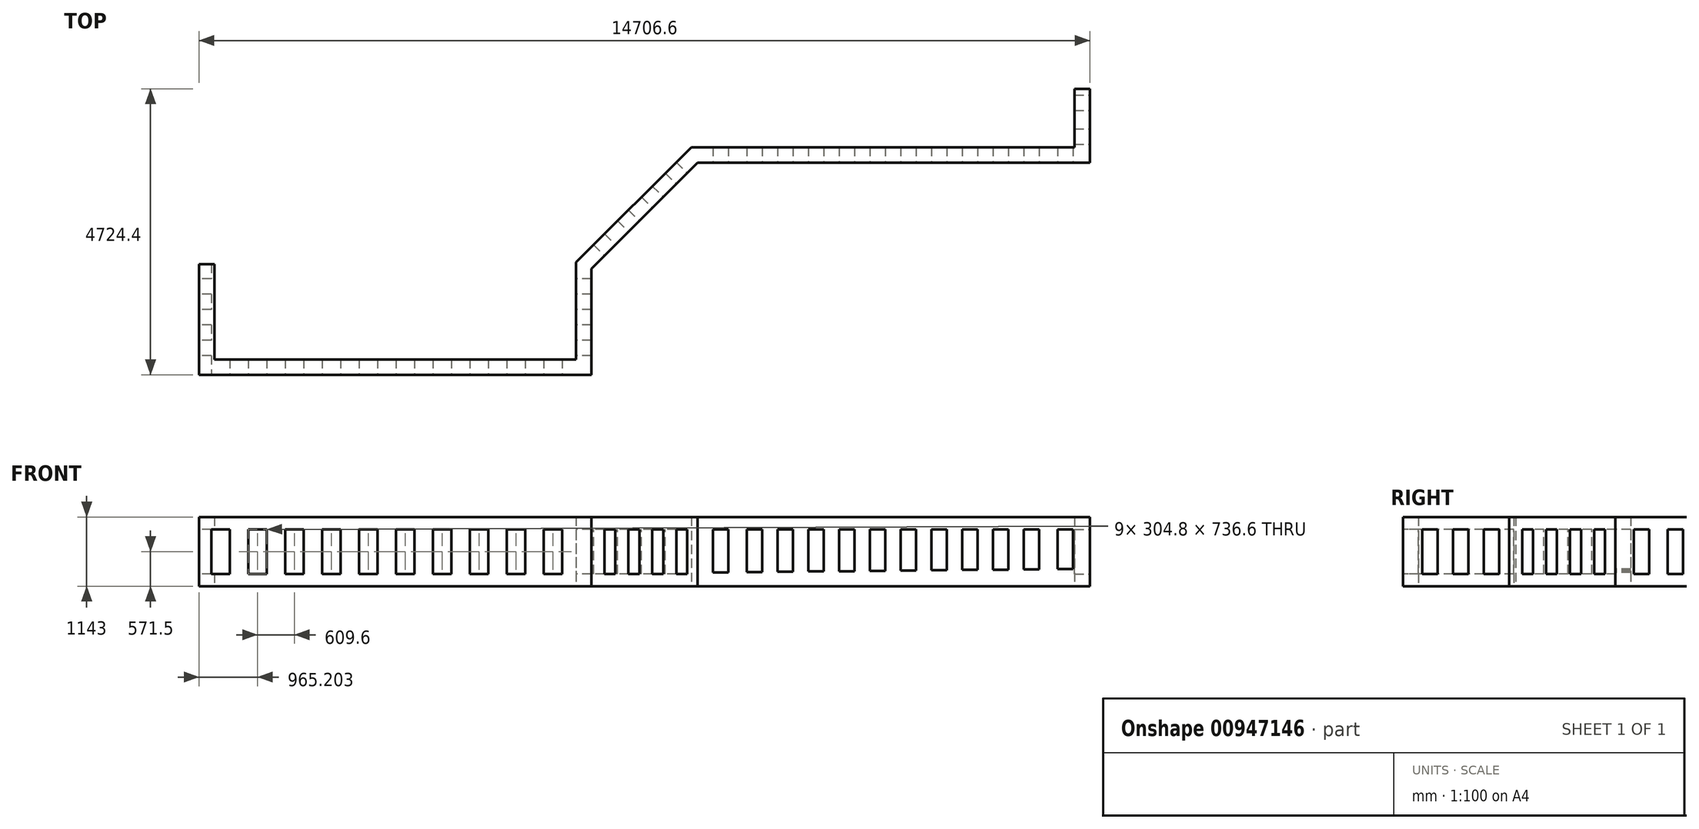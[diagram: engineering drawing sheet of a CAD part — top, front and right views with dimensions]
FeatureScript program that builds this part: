
annotation { "Feature Type Name" : "Feature", "Feature Type Description" : "" }
export const myFeature = defineFeature(function(context is Context, id is Id, definition is map)
    precondition{}
    {
        {
            var Q0;
            Q0=qCreatedBy(makeId("Top.planeOp"),FACE);
            var sketch = newSketch(context, id + "F0", { "sketchPlane" : qUnion([Q0])});
            skLineSegment(sketch, "E0.bottom", {"start": v(-9577.35, -1588.74) * mm, "end": v(-3100.35, -1588.74) * mm});
            skLineSegment(sketch, "E0.top", {"start": v(-9323.35, -1334.74) * mm, "end": v(-3354.35, -1334.74) * mm});
            skLineSegment(sketch, "E0.left", {"start": v(-9577.35, -1588.74) * mm, "end": v(-9577.35, -1334.74) * mm});
            skLineSegment(sketch, "E1.left", {"start": v(-3100.35, -1588.74) * mm, "end": v(-3100.35, 163.86) * mm});
            skLineSegment(sketch, "E2.top", {"start": v(-1347.75, 1916.46) * mm, "end": v(5129.25, 1916.46) * mm});
            skLineSegment(sketch, "E3", {"start": v(-3354.35, -1334.74) * mm, "end": v(-3354.35, 269.07) * mm});
            skLineSegment(sketch, "E4", {"start": v(-1347.75, 1916.46) * mm, "end": v(-3100.35, 163.86) * mm});
            skLineSegment(sketch, "E5", {"start": v(4875.25, 2170.46) * mm, "end": v(-1452.96, 2170.46) * mm});
            skLineSegment(sketch, "E6", {"start": v(-3354.35, 269.07) * mm, "end": v(-1452.96, 2170.46) * mm});
            skLineSegment(sketch, "E7.bottom", {"start": v(-9577.35, -1588.74) * mm, "end": v(-9323.35, -1588.74) * mm});
            skLineSegment(sketch, "E7.top", {"start": v(-9577.35, 240.06) * mm, "end": v(-9323.35, 240.06) * mm});
            skLineSegment(sketch, "E7.left", {"start": v(-9577.35, -1334.74) * mm, "end": v(-9577.35, 240.06) * mm});
            skLineSegment(sketch, "E7.right", {"start": v(-9323.35, -1334.74) * mm, "end": v(-9323.35, 240.06) * mm});
            skLineSegment(sketch, "E8.top", {"start": v(5129.25, 3135.66) * mm, "end": v(4875.25, 3135.66) * mm});
            skLineSegment(sketch, "E8.left", {"start": v(5129.25, 1916.46) * mm, "end": v(5129.25, 3135.66) * mm});
            skLineSegment(sketch, "E8.right", {"start": v(4875.25, 2170.46) * mm, "end": v(4875.25, 3135.66) * mm});
            skSolve(sketch);
        }
        {
            var Q0;
            Q0=makeQuery(id+"F0.imprint","IMPRINT",FACE,{"disambiguationData":[TD([[makeQuery(id+"F0.imprint","IMPRINT",EDGE,{"derivedFrom":sQuery(id+"F0.wireOp",EDGE,"E0.top")}),-1.0]])]});
            extrude(context, id + "F1", {"entities" : qUnion([Q0]), "depth" : 1143 * mm, "offsetDistance" : 25.4 * mm});
        }
        {
            var Q0;
            Q0=makeQuery(id+"F1.opExtrude","SWEPT_FACE",FACE,{"disambiguationData":[OSD([sQuery(id+"F0.wireOp",EDGE,"E0.bottom")])]});
            var sketch = newSketch(context, id + "F2", { "sketchPlane" : qUnion([Q0])});
            skLineSegment(sketch, "E9.bottom", {"start": v(-9374.15, 939.8) * mm, "end": v(-9069.35, 939.8) * mm});
            skLineSegment(sketch, "E9.top", {"start": v(-9374.15, 203.2) * mm, "end": v(-9069.35, 203.2) * mm});
            skLineSegment(sketch, "E9.left", {"start": v(-9374.15, 939.8) * mm, "end": v(-9374.15, 203.2) * mm});
            skLineSegment(sketch, "E9.right", {"start": v(-9069.35, 939.8) * mm, "end": v(-9069.35, 203.2) * mm});
            skLineSegment(sketch, "E10.1.0.0", {"start": v(-8459.75, 939.8) * mm, "end": v(-8459.75, 203.2) * mm});
            skLineSegment(sketch, "E10.1.0.1", {"start": v(-8764.55, 939.8) * mm, "end": v(-8764.55, 203.2) * mm});
            skLineSegment(sketch, "E10.2.0.0", {"start": v(-7850.15, 939.8) * mm, "end": v(-7850.15, 203.2) * mm});
            skLineSegment(sketch, "E10.2.0.1", {"start": v(-8154.95, 939.8) * mm, "end": v(-8154.95, 203.2) * mm});
            skLineSegment(sketch, "E10.3.0.0", {"start": v(-7240.55, 939.8) * mm, "end": v(-7240.55, 203.2) * mm});
            skLineSegment(sketch, "E10.3.0.1", {"start": v(-7545.35, 939.8) * mm, "end": v(-7545.35, 203.2) * mm});
            skLineSegment(sketch, "E10.4.0.0", {"start": v(-6630.95, 939.8) * mm, "end": v(-6630.95, 203.2) * mm});
            skLineSegment(sketch, "E10.4.0.1", {"start": v(-6935.75, 939.8) * mm, "end": v(-6935.75, 203.2) * mm});
            skLineSegment(sketch, "E10.5.0.0", {"start": v(-6021.35, 939.8) * mm, "end": v(-6021.35, 203.2) * mm});
            skLineSegment(sketch, "E10.5.0.1", {"start": v(-6326.15, 939.8) * mm, "end": v(-6326.15, 203.2) * mm});
            skLineSegment(sketch, "E10.6.0.0", {"start": v(-5411.75, 939.8) * mm, "end": v(-5411.75, 203.2) * mm});
            skLineSegment(sketch, "E10.6.0.1", {"start": v(-5716.55, 939.8) * mm, "end": v(-5716.55, 203.2) * mm});
            skLineSegment(sketch, "E10.7.0.0", {"start": v(-4802.15, 939.8) * mm, "end": v(-4802.15, 203.2) * mm});
            skLineSegment(sketch, "E10.7.0.1", {"start": v(-5106.95, 939.8) * mm, "end": v(-5106.95, 203.2) * mm});
            skLineSegment(sketch, "E10.8.0.0", {"start": v(-4192.55, 939.8) * mm, "end": v(-4192.55, 203.2) * mm});
            skLineSegment(sketch, "E10.8.0.1", {"start": v(-4497.35, 939.8) * mm, "end": v(-4497.35, 203.2) * mm});
            skLineSegment(sketch, "E10.9.0.0", {"start": v(-3582.95, 939.8) * mm, "end": v(-3582.95, 203.2) * mm});
            skLineSegment(sketch, "E10.9.0.1", {"start": v(-3887.75, 939.8) * mm, "end": v(-3887.75, 203.2) * mm});
            skLineSegment(sketch, "E11", {"start": v(-8764.55, 939.8) * mm, "end": v(-8459.75, 939.8) * mm});
            skLineSegment(sketch, "E12", {"start": v(-8764.55, 203.2) * mm, "end": v(-8459.75, 203.2) * mm});
            skPoint(sketch, "E13.orphan", {"position": v(-8991.86, 203.2) * mm});
            skLineSegment(sketch, "E14.trimOffspring", {"start": v(-8154.95, 203.2) * mm, "end": v(-7850.15, 203.2) * mm});
            skLineSegment(sketch, "E15.trimOffspring", {"start": v(-8154.95, 939.8) * mm, "end": v(-7850.15, 939.8) * mm});
            skLineSegment(sketch, "E16.trimOffspring", {"start": v(-7545.35, 939.8) * mm, "end": v(-7240.55, 939.8) * mm});
            skLineSegment(sketch, "E17.trimOffspring", {"start": v(-7545.35, 203.2) * mm, "end": v(-7240.55, 203.2) * mm});
            skLineSegment(sketch, "E18.trimOffspring", {"start": v(-6935.75, 203.2) * mm, "end": v(-6630.95, 203.2) * mm});
            skLineSegment(sketch, "E19.trimOffspring", {"start": v(-6935.75, 939.8) * mm, "end": v(-6630.95, 939.8) * mm});
            skLineSegment(sketch, "E20.trimOffspring", {"start": v(-6326.15, 939.8) * mm, "end": v(-6021.35, 939.8) * mm});
            skLineSegment(sketch, "E21.trimOffspring", {"start": v(-6326.15, 203.2) * mm, "end": v(-6021.35, 203.2) * mm});
            skLineSegment(sketch, "E22.trimOffspring", {"start": v(-5716.55, 203.2) * mm, "end": v(-5411.75, 203.2) * mm});
            skLineSegment(sketch, "E23.trimOffspring", {"start": v(-5716.55, 939.8) * mm, "end": v(-5411.75, 939.8) * mm});
            skLineSegment(sketch, "E24.trimOffspring", {"start": v(-5106.95, 939.8) * mm, "end": v(-4802.15, 939.8) * mm});
            skLineSegment(sketch, "E25.trimOffspring", {"start": v(-5106.95, 203.2) * mm, "end": v(-4802.15, 203.2) * mm});
            skLineSegment(sketch, "E26.trimOffspring", {"start": v(-4497.35, 203.2) * mm, "end": v(-4192.55, 203.2) * mm});
            skLineSegment(sketch, "E27.trimOffspring", {"start": v(-4497.35, 939.8) * mm, "end": v(-4192.55, 939.8) * mm});
            skLineSegment(sketch, "E28.trimOffspring", {"start": v(-3887.75, 939.8) * mm, "end": v(-3582.95, 939.8) * mm});
            skLineSegment(sketch, "E29.trimOffspring", {"start": v(-3887.75, 203.2) * mm, "end": v(-3582.95, 203.2) * mm});
            skLineSegment(sketch, "E30", {"start": v(-3582.95, 939.8) * mm, "end": v(5273.77, 939.8) * mm, "construction": true});
            skLineSegment(sketch, "E31", {"start": v(-3582.95, 203.2) * mm, "end": v(5279.33, 288.16) * mm, "construction": true});
            skLineSegment(sketch, "E32.bottom", {"start": v(-1093.75, 939.8) * mm, "end": v(-839.75, 939.8) * mm});
            skLineSegment(sketch, "E32.top", {"start": v(-1093.75, 229.5) * mm, "end": v(-839.75, 229.5) * mm});
            skLineSegment(sketch, "E32.left", {"start": v(-1093.75, 939.8) * mm, "end": v(-1093.75, 229.5) * mm});
            skLineSegment(sketch, "E32.right", {"start": v(-839.75, 939.8) * mm, "end": v(-839.75, 229.5) * mm});
            skLineSegment(sketch, "E33.bottom", {"start": v(-534.95, 939.8) * mm, "end": v(-280.95, 939.8) * mm});
            skLineSegment(sketch, "E33.top", {"start": v(-534.95, 234.86) * mm, "end": v(-280.95, 234.86) * mm});
            skLineSegment(sketch, "E33.left", {"start": v(-534.95, 939.8) * mm, "end": v(-534.95, 234.86) * mm});
            skLineSegment(sketch, "E33.right", {"start": v(-280.95, 939.8) * mm, "end": v(-280.95, 234.86) * mm});
            skLineSegment(sketch, "E34.bottom", {"start": v(-26.95, 939.8) * mm, "end": v(227.05, 939.8) * mm});
            skLineSegment(sketch, "E34.top", {"start": v(-26.95, 239.73) * mm, "end": v(227.05, 239.73) * mm});
            skLineSegment(sketch, "E34.left", {"start": v(-26.95, 939.8) * mm, "end": v(-26.95, 239.73) * mm});
            skLineSegment(sketch, "E34.right", {"start": v(227.05, 939.8) * mm, "end": v(227.05, 239.73) * mm});
            skLineSegment(sketch, "E35.bottom", {"start": v(481.05, 939.8) * mm, "end": v(735.05, 939.8) * mm});
            skLineSegment(sketch, "E35.top", {"start": v(481.05, 244.6) * mm, "end": v(735.05, 244.6) * mm});
            skLineSegment(sketch, "E35.left", {"start": v(481.05, 939.8) * mm, "end": v(481.05, 244.6) * mm});
            skLineSegment(sketch, "E35.right", {"start": v(735.05, 939.8) * mm, "end": v(735.05, 244.6) * mm});
            skLineSegment(sketch, "E36.bottom", {"start": v(989.05, 939.8) * mm, "end": v(1243.05, 939.8) * mm});
            skLineSegment(sketch, "E36.top", {"start": v(989.05, 249.47) * mm, "end": v(1243.05, 249.47) * mm});
            skLineSegment(sketch, "E36.left", {"start": v(989.05, 939.8) * mm, "end": v(989.05, 249.47) * mm});
            skLineSegment(sketch, "E36.right", {"start": v(1243.05, 939.8) * mm, "end": v(1243.05, 249.47) * mm});
            skLineSegment(sketch, "E37.bottom", {"start": v(1497.05, 939.8) * mm, "end": v(1751.05, 939.8) * mm});
            skLineSegment(sketch, "E37.top", {"start": v(1497.05, 254.34) * mm, "end": v(1751.05, 254.34) * mm});
            skLineSegment(sketch, "E37.left", {"start": v(1497.05, 939.8) * mm, "end": v(1497.05, 254.34) * mm});
            skLineSegment(sketch, "E37.right", {"start": v(1751.05, 939.8) * mm, "end": v(1751.05, 254.34) * mm});
            skLineSegment(sketch, "E38.bottom", {"start": v(2005.05, 939.8) * mm, "end": v(2259.05, 939.8) * mm});
            skLineSegment(sketch, "E38.top", {"start": v(2005.05, 259.2) * mm, "end": v(2259.05, 259.2) * mm});
            skLineSegment(sketch, "E38.left", {"start": v(2005.05, 939.8) * mm, "end": v(2005.05, 259.2) * mm});
            skLineSegment(sketch, "E38.right", {"start": v(2259.05, 939.8) * mm, "end": v(2259.05, 259.2) * mm});
            skLineSegment(sketch, "E39.bottom", {"start": v(2513.05, 939.8) * mm, "end": v(2767.05, 939.8) * mm});
            skLineSegment(sketch, "E39.top", {"start": v(2513.05, 264.08) * mm, "end": v(2767.05, 264.08) * mm});
            skLineSegment(sketch, "E39.left", {"start": v(2513.05, 939.8) * mm, "end": v(2513.05, 264.08) * mm});
            skLineSegment(sketch, "E39.right", {"start": v(2767.05, 939.8) * mm, "end": v(2767.05, 264.08) * mm});
            skLineSegment(sketch, "E40.bottom", {"start": v(3021.05, 939.8) * mm, "end": v(3275.05, 939.8) * mm});
            skLineSegment(sketch, "E40.top", {"start": v(3021.05, 268.95) * mm, "end": v(3275.05, 268.95) * mm});
            skLineSegment(sketch, "E40.left", {"start": v(3021.05, 939.8) * mm, "end": v(3021.05, 268.95) * mm});
            skLineSegment(sketch, "E40.right", {"start": v(3275.05, 939.8) * mm, "end": v(3275.05, 268.95) * mm});
            skLineSegment(sketch, "E41.bottom", {"start": v(3529.05, 939.8) * mm, "end": v(3783.05, 939.8) * mm});
            skLineSegment(sketch, "E41.top", {"start": v(3529.05, 273.82) * mm, "end": v(3783.05, 273.82) * mm});
            skLineSegment(sketch, "E41.left", {"start": v(3529.05, 939.8) * mm, "end": v(3529.05, 273.82) * mm});
            skLineSegment(sketch, "E41.right", {"start": v(3783.05, 939.8) * mm, "end": v(3783.05, 273.82) * mm});
            skLineSegment(sketch, "E42.bottom", {"start": v(4037.05, 939.8) * mm, "end": v(4291.05, 939.8) * mm});
            skLineSegment(sketch, "E42.top", {"start": v(4037.05, 278.69) * mm, "end": v(4291.05, 278.69) * mm});
            skLineSegment(sketch, "E42.left", {"start": v(4037.05, 939.8) * mm, "end": v(4037.05, 278.69) * mm});
            skLineSegment(sketch, "E42.right", {"start": v(4291.05, 939.8) * mm, "end": v(4291.05, 278.69) * mm});
            skLineSegment(sketch, "E43.bottom", {"start": v(4595.85, 939.8) * mm, "end": v(4849.85, 939.8) * mm});
            skLineSegment(sketch, "E43.top", {"start": v(4595.85, 284.04) * mm, "end": v(4849.85, 284.04) * mm});
            skLineSegment(sketch, "E43.left", {"start": v(4595.85, 939.8) * mm, "end": v(4595.85, 284.04) * mm});
            skLineSegment(sketch, "E43.right", {"start": v(4849.85, 939.8) * mm, "end": v(4849.85, 284.04) * mm});
            skSolve(sketch);
        }
        {
            var Q0;
            Q0 = qSketchRegion(id + "F2", true);
            extrude(context, id + "F3", {"entities" : qUnion([Q0]), "operationType" : NewBodyOperationType.REMOVE, "oppositeDirection" : true, "depth" : 4734.56 * mm, "offsetDistance" : 25.4 * mm});
        }
        {
            var Q0;
            Q0=makeQuery(id+"F1.opExtrude","SWEPT_FACE",FACE,{"disambiguationData":[OSD([sQuery(id+"F0.wireOp",EDGE,"E4")])]});
            var sketch = newSketch(context, id + "F4", { "sketchPlane" : qUnion([Q0])});
            skLineSegment(sketch, "E44", {"start": v(-4292.04, 939.8) * mm, "end": v(1866.41, 939.8) * mm, "construction": true});
            skLineSegment(sketch, "E45", {"start": v(1685.1, 203.2) * mm, "end": v(-4720.32, 203.2) * mm, "construction": true});
            skLineSegment(sketch, "E46.bottom", {"start": v(-1771.61, 939.8) * mm, "end": v(-1517.61, 939.8) * mm});
            skLineSegment(sketch, "E46.top", {"start": v(-1771.61, 203.2) * mm, "end": v(-1517.61, 203.2) * mm});
            skLineSegment(sketch, "E46.left", {"start": v(-1771.61, 939.8) * mm, "end": v(-1771.61, 203.2) * mm});
            skLineSegment(sketch, "E46.right", {"start": v(-1517.61, 939.8) * mm, "end": v(-1517.61, 203.2) * mm});
            skLineSegment(sketch, "E47.bottom", {"start": v(-1212.81, 939.8) * mm, "end": v(-958.81, 939.8) * mm});
            skLineSegment(sketch, "E47.top", {"start": v(-1212.81, 203.2) * mm, "end": v(-958.81, 203.2) * mm});
            skLineSegment(sketch, "E47.left", {"start": v(-1212.81, 939.8) * mm, "end": v(-1212.81, 203.2) * mm});
            skLineSegment(sketch, "E47.right", {"start": v(-958.81, 939.8) * mm, "end": v(-958.81, 203.2) * mm});
            skLineSegment(sketch, "E48.bottom", {"start": v(-654.01, 939.8) * mm, "end": v(-400.01, 939.8) * mm});
            skLineSegment(sketch, "E48.top", {"start": v(-654.01, 203.2) * mm, "end": v(-400.01, 203.2) * mm});
            skLineSegment(sketch, "E48.left", {"start": v(-654.01, 939.8) * mm, "end": v(-654.01, 203.2) * mm});
            skLineSegment(sketch, "E48.right", {"start": v(-400.01, 939.8) * mm, "end": v(-400.01, 203.2) * mm});
            skLineSegment(sketch, "E49.bottom", {"start": v(-95.21, 939.8) * mm, "end": v(158.79, 939.8) * mm});
            skLineSegment(sketch, "E49.top", {"start": v(-95.21, 203.2) * mm, "end": v(158.79, 203.2) * mm});
            skLineSegment(sketch, "E49.left", {"start": v(-95.21, 939.8) * mm, "end": v(-95.21, 203.2) * mm});
            skLineSegment(sketch, "E49.right", {"start": v(158.79, 939.8) * mm, "end": v(158.79, 203.2) * mm});
            skSolve(sketch);
        }
        {
            var Q0;
            Q0 = qSketchRegion(id + "F4", true);
            extrude(context, id + "F5", {"entities" : qUnion([Q0]), "operationType" : NewBodyOperationType.REMOVE, "oppositeDirection" : true, "depth" : 584.2 * mm, "offsetDistance" : 25.4 * mm});
        }
        {
            var Q0;
            Q0=makeQuery(id+"F1.opExtrude","SWEPT_FACE",FACE,{"disambiguationData":[OSD([sQuery(id+"F0.wireOp",EDGE,"E0.left"),sQuery(id+"F0.wireOp",EDGE,"E7.left")])]});
            var sketch = newSketch(context, id + "F6", { "sketchPlane" : qUnion([Q0])});
            skLineSegment(sketch, "E50", {"start": v(-1062.62, 939.8) * mm, "end": v(2731.13, 939.8) * mm, "construction": true});
            skLineSegment(sketch, "E51", {"start": v(-1201.98, 203.2) * mm, "end": v(2731.13, 203.2) * mm, "construction": true});
            skLineSegment(sketch, "E52.bottom", {"start": v(0, 939.8) * mm, "end": v(254, 939.8) * mm});
            skLineSegment(sketch, "E52.top", {"start": v(0, 203.2) * mm, "end": v(254, 203.2) * mm});
            skLineSegment(sketch, "E52.left", {"start": v(0, 939.8) * mm, "end": v(0, 203.2) * mm});
            skLineSegment(sketch, "E52.right", {"start": v(254, 939.8) * mm, "end": v(254, 203.2) * mm});
            skLineSegment(sketch, "E53.bottom", {"start": v(508, 939.8) * mm, "end": v(762, 939.8) * mm});
            skLineSegment(sketch, "E53.top", {"start": v(508, 203.2) * mm, "end": v(762, 203.2) * mm});
            skLineSegment(sketch, "E53.left", {"start": v(508, 939.8) * mm, "end": v(508, 203.2) * mm});
            skLineSegment(sketch, "E53.right", {"start": v(762, 939.8) * mm, "end": v(762, 203.2) * mm});
            skLineSegment(sketch, "E54.bottom", {"start": v(1016, 939.8) * mm, "end": v(1270, 939.8) * mm});
            skLineSegment(sketch, "E54.top", {"start": v(1016, 203.2) * mm, "end": v(1270, 203.2) * mm});
            skLineSegment(sketch, "E54.left", {"start": v(1016, 939.8) * mm, "end": v(1016, 203.2) * mm});
            skLineSegment(sketch, "E54.right", {"start": v(1270, 939.8) * mm, "end": v(1270, 203.2) * mm});
            skSolve(sketch);
        }
        {
            var Q0;
            Q0 = qSketchRegion(id + "F6", true);
            extrude(context, id + "F7", {"entities" : qUnion([Q0]), "operationType" : NewBodyOperationType.REMOVE, "oppositeDirection" : true, "depth" : 7112 * mm, "offsetDistance" : 25.4 * mm});
        }
        {
            var Q0;
            Q0=makeQuery(id+"F1.opExtrude","SWEPT_FACE",FACE,{"disambiguationData":[OSD([sQuery(id+"F0.wireOp",EDGE,"E8.left")])]});
            var sketch = newSketch(context, id + "F8", { "sketchPlane" : qUnion([Q0])});
            skLineSegment(sketch, "E55", {"start": v(1536.36, 939.8) * mm, "end": v(3271.26, 939.8) * mm, "construction": true});
            skLineSegment(sketch, "E56", {"start": v(1733.42, 203.2) * mm, "end": v(3271.26, 203.2) * mm, "construction": true});
            skLineSegment(sketch, "E57.bottom", {"start": v(2221.26, 939.8) * mm, "end": v(2475.26, 939.8) * mm});
            skLineSegment(sketch, "E57.top", {"start": v(2221.26, 203.2) * mm, "end": v(2475.26, 203.2) * mm});
            skLineSegment(sketch, "E57.left", {"start": v(2221.26, 939.8) * mm, "end": v(2221.26, 203.2) * mm});
            skLineSegment(sketch, "E57.right", {"start": v(2475.26, 939.8) * mm, "end": v(2475.26, 203.2) * mm});
            skLineSegment(sketch, "E58.bottom", {"start": v(2780.06, 939.8) * mm, "end": v(3034.06, 939.8) * mm});
            skLineSegment(sketch, "E58.top", {"start": v(2780.06, 203.2) * mm, "end": v(3034.06, 203.2) * mm});
            skLineSegment(sketch, "E58.left", {"start": v(2780.06, 939.8) * mm, "end": v(2780.06, 203.2) * mm});
            skLineSegment(sketch, "E58.right", {"start": v(3034.06, 939.8) * mm, "end": v(3034.06, 203.2) * mm});
            skLineSegment(sketch, "E59.bottom", {"start": v(2845.71, 939.8) * mm, "end": v(3011.2, 939.8) * mm});
            skLineSegment(sketch, "E59.top", {"start": v(2845.71, 203.2) * mm, "end": v(3011.2, 203.2) * mm});
            skSolve(sketch);
        }
        {
            var Q0;
            {var subQ7=sQuery(id+"F8.wireOp",EDGE,"E58.left");Q0=qUnion([makeQuery(id+"F8.imprint","IMPRINT",FACE,{"disambiguationData":[TD([[makeQuery(id+"F8.imprint","IMPRINT",EDGE,{"derivedFrom":sQuery(id+"F8.wireOp",EDGE,"E57.bottom")}),-1.0]])]}),makeQuery(id+"F8.imprint","IMPRINT",FACE,{"disambiguationData":[TD([[makeQuery(id+"F8.imprint","IMPRINT",EDGE,{"derivedFrom":subQ7}),1.0]])]})]);}
            extrude(context, id + "F9", {"entities" : qUnion([Q0]), "operationType" : NewBodyOperationType.REMOVE, "oppositeDirection" : true, "depth" : 304.8 * mm, "offsetDistance" : 25.4 * mm});
        }
    });
